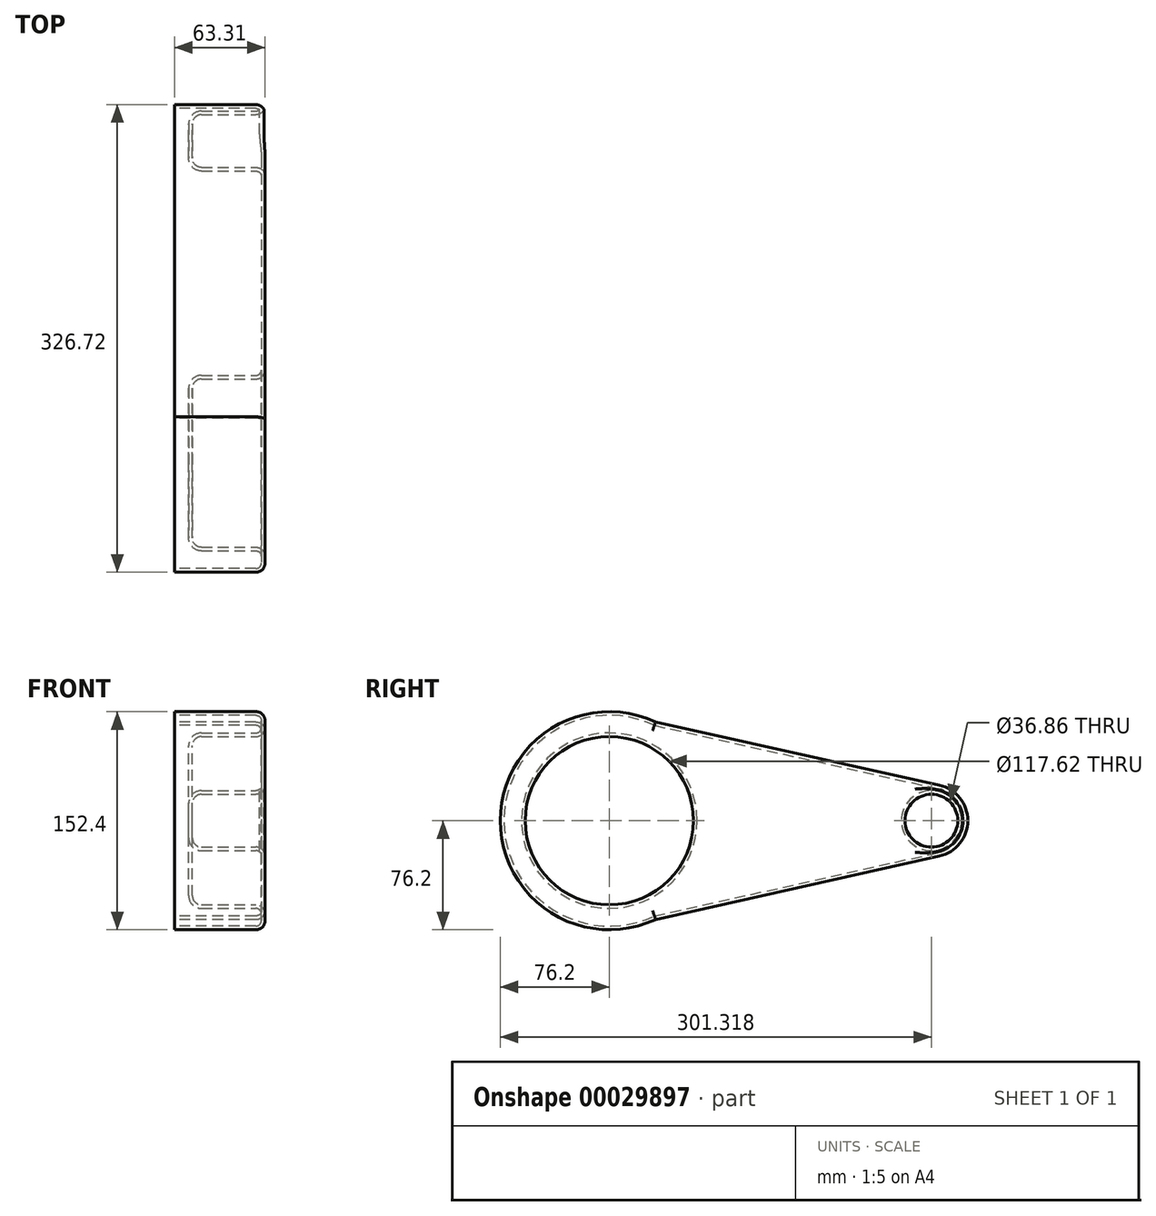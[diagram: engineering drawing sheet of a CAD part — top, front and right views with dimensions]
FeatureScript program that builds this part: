
annotation { "Feature Type Name" : "Feature", "Feature Type Description" : "" }
export const myFeature = defineFeature(function(context is Context, id is Id, definition is map)
    precondition{}
    {
        {
            var Q0;
            Q0=qCreatedBy(makeId("Right.planeOp"),FACE);
            var sketch = newSketch(context, id + "F0", { "sketchPlane" : qUnion([Q0])});
            skCircle(sketch, "E0", {"center": v(0, 0) * mm, "radius": 76.2 * mm});
            skCircle(sketch, "E1", {"center": v(225.12, 0) * mm, "radius": 25.4 * mm});
            skLineSegment(sketch, "E2", {"start": v(32.31, 69) * mm, "end": v(230.65, 24.8) * mm});
            skLineSegment(sketch, "E3", {"start": v(32.31, -69) * mm, "end": v(230.65, -24.8) * mm});
            skSolve(sketch);
        }
        {
            var Q0;
            {var subQ0=sQuery(id+"F0.wireOp",EDGE,"E0");var subQ2=makeQuery(id+"F0.imprint","INTERSECT",VERTEX,{"derivedFrom":[subQ0,sQuery(id+"F0.wireOp",EDGE,"E2")]});Q0=makeQuery(id+"F0.imprint","IMPRINT",FACE,{"disambiguationData":[TD([[makeQuery(id+"F0.imprint","IMPRINT",EDGE,{"disambiguationData":[TD([[subQ2,-1.0]])],"derivedFrom":subQ0}),1.0]])]});}
            var Q1;
            {var subQ1=sQuery(id+"F0.wireOp",EDGE,"E2");Q1=makeQuery(id+"F0.imprint","IMPRINT",FACE,{"disambiguationData":[TD([[makeQuery(id+"F0.imprint","IMPRINT",EDGE,{"derivedFrom":subQ1}),-1.0]])]});}
            var Q2;
            {var subQ0=sQuery(id+"F0.wireOp",EDGE,"E1");var subQ2=makeQuery(id+"F0.imprint","INTERSECT",VERTEX,{"derivedFrom":[subQ0,sQuery(id+"F0.wireOp",EDGE,"E2")]});Q2=makeQuery(id+"F0.imprint","IMPRINT",FACE,{"disambiguationData":[TD([[makeQuery(id+"F0.imprint","IMPRINT",EDGE,{"disambiguationData":[TD([[subQ2,-1.0]])],"derivedFrom":subQ0}),1.0]])]});}
            extrude(context, id + "F1", {"entities" : qUnion([Q0, Q1, Q2]), "depth" : 63.31 * mm, "hasSecondDirectionDraft" : true, "secondDirectionDraftAngle" : 3 * degree});
        }
        {
            var Q0;
            Q0=makeQuery(id+"F1.opExtrude","CAP_FACE",FACE,{"disambiguationData":[OSD([sQuery(id+"F0.wireOp",EDGE,"E0"),sQuery(id+"F0.wireOp",EDGE,"E1"),sQuery(id+"F0.wireOp",EDGE,"E2"),sQuery(id+"F0.wireOp",EDGE,"E3")])],"isStart":false});
            var sketch = newSketch(context, id + "F2", { "sketchPlane" : qUnion([Q0])});
            skCircle(sketch, "E4", {"center": v(0, 0) * mm, "radius": 58.8 * mm});
            skCircle(sketch, "E5", {"center": v(225.12, 0) * mm, "radius": 18.43 * mm});
            skSolve(sketch);
        }
        {
            var Q0;
            Q0=makeQuery(id+"F2.imprint","IMPRINT",FACE,{"disambiguationData":[TD([[makeQuery(id+"F2.imprint","IMPRINT",EDGE,{"derivedFrom":sQuery(id+"F2.wireOp",EDGE,"E4")}),1.0]])]});
            var Q1;
            Q1=makeQuery(id+"F2.imprint","IMPRINT",FACE,{"disambiguationData":[TD([[makeQuery(id+"F2.imprint","IMPRINT",EDGE,{"derivedFrom":sQuery(id+"F2.wireOp",EDGE,"E5")}),1.0]])]});
            extrude(context, id + "F3", {"entities" : qUnion([Q0, Q1]), "operationType" : NewBodyOperationType.REMOVE, "oppositeDirection" : true, "depth" : 50.8 * mm});
        }
        {
            var Q0;
            Q0=makeQuery(id+"F3.boolean.opBoolean","COPY",FACE,{"derivedFrom":makeQuery(id+"F3.opExtrude","CAP_FACE",FACE,{"disambiguationData":[OSD([sQuery(id+"F2.wireOp",EDGE,"E4")])],"isStart":false})});
            var Q1;
            Q1=makeQuery(id+"F3.boolean.opBoolean","COPY",FACE,{"derivedFrom":makeQuery(id+"F3.opExtrude","CAP_FACE",FACE,{"disambiguationData":[OSD([sQuery(id+"F2.wireOp",EDGE,"E5")])],"isStart":false})});
            var Q2;
            Q2=makeQuery(id+"F1.opExtrude","CAP_FACE",FACE,{"disambiguationData":[OSD([sQuery(id+"F0.wireOp",EDGE,"E0"),sQuery(id+"F0.wireOp",EDGE,"E1"),sQuery(id+"F0.wireOp",EDGE,"E2"),sQuery(id+"F0.wireOp",EDGE,"E3")])],"isStart":false});
            fillet(context, id + "F4", {"entities" : qUnion([Q0, Q1, Q2]), "radius" : 6.35 * mm, "tangentPropagation" : true, "allowEdgeOverflow" : false});
        }
        {
            var Q0;
            Q0=makeQuery(id+"F1.opExtrude","CAP_FACE",FACE,{"disambiguationData":[OSD([sQuery(id+"F0.wireOp",EDGE,"E0"),sQuery(id+"F0.wireOp",EDGE,"E1"),sQuery(id+"F0.wireOp",EDGE,"E2"),sQuery(id+"F0.wireOp",EDGE,"E3")])],"isStart":true});
            shell(context, id + "F5", {"entities" : qUnion([Q0]), "thickness" : 2.54 * mm});
        }
    });
